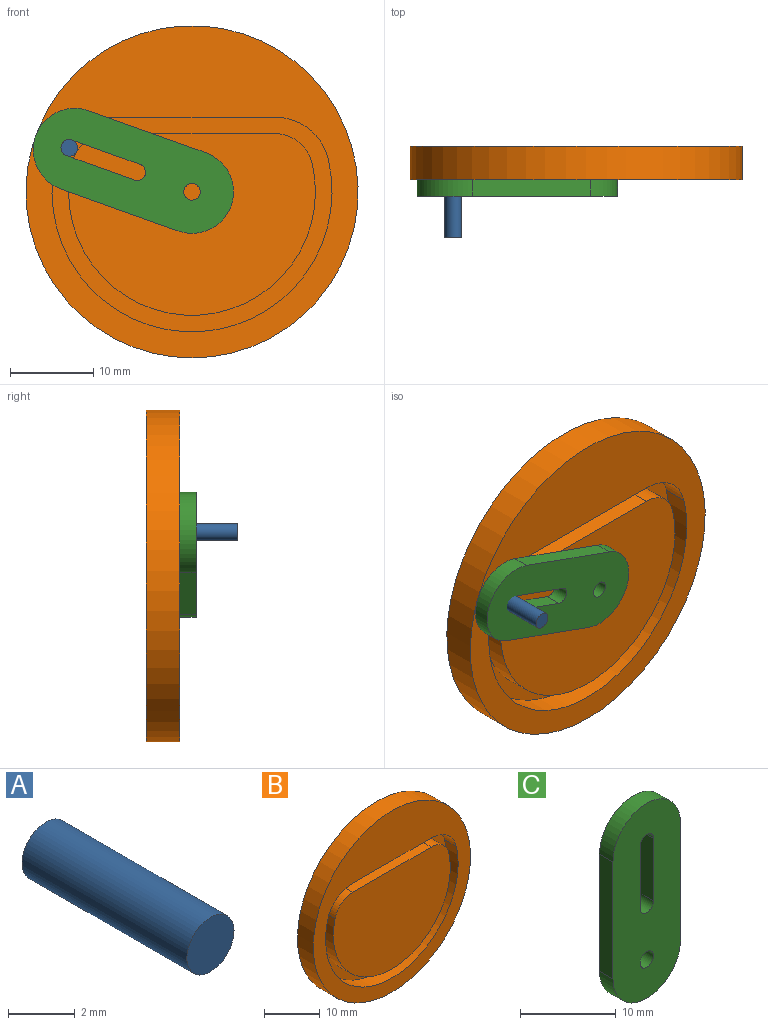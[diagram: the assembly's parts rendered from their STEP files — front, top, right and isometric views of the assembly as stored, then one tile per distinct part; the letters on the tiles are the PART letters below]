
ASSEMBLY  parts=3 mates=2
PART A: 3 faces, bbox 2x7x2 mm
  f0: cylinder r=1mm len=7mm, axis (0,1,0), area 44mm2, adj f1,f2
  f1: plane 2x2mm, normal (0,-1,0), area 3.1mm2, adj f0
  f2: plane 2x2mm, normal (0,1,0), area 3.1mm2, adj f0
PART B: 13 faces, bbox 40x4x40 mm
  f0: cylinder r=20mm len=40mm, axis (0,-1,0), area 502.7mm2, adj f1,f2
  f1: plane 40x40mm, normal (0,1,0), area 1256.6mm2, adj f0
  f2: plane 40x40mm, normal (0,-1,0), area 528.7mm2, adj f0,f3,f4,f5,f10
  f3: cylinder r=16.87mm len=33.73mm, axis (0,-1,0), area 183mm2, adj f2,f4,f10,f11
  f4: cylinder r=6.58mm len=6.39mm, axis (0,-1,0), area 26.3mm2, adj f2,f3,f5,f11
  f5: plane 20x3mm, normal (0,0,-1), area 60mm2, adj f2,f4,f10,f11
  f6: cylinder r=4.58mm len=4.45mm, axis (0,-1,0), area 18.3mm2, adj f7,f9,f11,f12
  f7: plane 20x3mm, normal (0,0,1), area 60mm2, adj f6,f8,f11,f12
  f8: cylinder r=4.58mm len=4.45mm, axis (0,-1,0), area 18.3mm2, adj f7,f9,f11,f12
  f9: cylinder r=14.87mm len=29.73mm, axis (0,-1,0), area 161.3mm2, adj f6,f8,f11,f12
  f10: cylinder r=6.58mm len=6.39mm, axis (0,-1,0), area 26.3mm2, adj f2,f3,f5,f11
  f11: plane 33.73x25.87mm, normal (0,-1,0), area 184.5mm2, adj f3,f4,f5,f6,f7,f8,f9,f10
  f12: plane 29.73x21.87mm, normal (0,-1,0), area 543.4mm2, adj f6,f7,f8,f9
PART C: 11 faces, bbox 10x2x25 mm
  f0: plane 8x2mm, normal (-1,0,0), area 16mm2, adj f1,f6,f9,f10
  f1: cylinder r=1mm len=2mm, axis (0,1,0), area 6.3mm2, adj f0,f2,f9,f10
  f2: plane 8x2mm, normal (1,0,0), area 16mm2, adj f1,f6,f9,f10
  f3: plane 15x2mm, normal (1,0,0), area 30mm2, adj f4,f7,f9,f10
  f4: cylinder r=5mm len=10mm, axis (0,1,0), area 31.4mm2, adj f3,f5,f9,f10
  f5: plane 15x2mm, normal (-1,0,0), area 30mm2, adj f4,f7,f9,f10
  f6: cylinder r=1mm len=2mm, axis (0,1,0), area 6.3mm2, adj f0,f2,f9,f10
  f7: cylinder r=5mm len=10mm, axis (0,1,0), area 31.4mm2, adj f3,f5,f9,f10
  f8: cylinder r=1mm len=2mm, axis (0,1,0), area 12.6mm2, adj f9,f10
  f9: plane 25x10mm, normal (0,-1,0), area 206.3mm2, adj f0,f1,f2,f3,f4,f5,f6,f7
  f10: plane 25x10mm, normal (0,1,0), area 206.3mm2, adj f0,f1,f2,f3,f4,f5,f6,f7
PLACE A rot(axis=(0.35,0,0.94),180deg) t=(-20.11,-6,-0.8)mm
PLACE B at identity fixed
PLACE C rot(axis=(0,-1,0),70.3deg) t=(0,0,0)mm
MATE pin_slot A.f0 <-> C.f10  axis (0,1,0) through (-14.78,0,5.3)mm
MATE revolute C.f8 <-> B.f0  axis (0,-1,0) through (0,-2,0)mm
